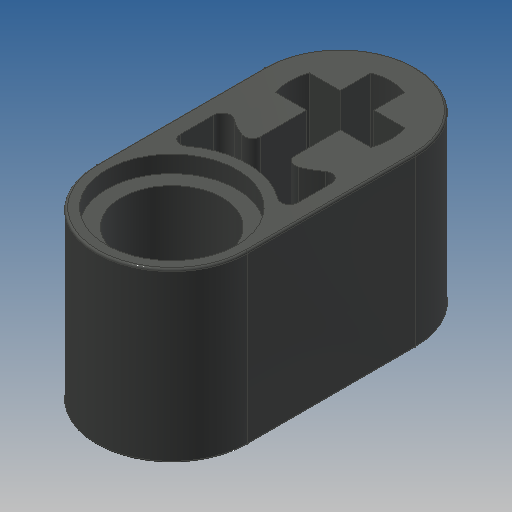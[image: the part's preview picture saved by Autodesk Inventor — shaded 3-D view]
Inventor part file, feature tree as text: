
AUTODESK INVENTOR PART (.ipt)
format: ipt  version: 2022.2 (Build 262287000, 287)  size: 195,072 bytes
history: native  units: mm
features: extrude x2, sketch x2, mirror x1, fillet x1
ambient origin geometry x8: Origin, YZ Plane, XZ Plane, XY Plane, X Axis, Y Axis, Z Axis, Center Point
bodies: Solid1 (feature_tree)
feature tree (6):
  extrude  "Extrusion1"  Depth=6.4mm
  extrude  "Extrusion7"  Depth=7.2mm
  mirror  "Mirror1"
  fillet  "Fillet1"  Radius=8.0mm
  sketch  "Sketch1"  dims[d8=4.8mm d9=6.4mm]
  sketch  "Sketch6"  dims[d14=8.0mm d15=0.0mm d32=7.2mm d34=8.0mm d36=0.8mm d41=0.8mm d42=0.0mm d45=0.1mm d46=0.4mm d52=1.6mm d53=6.2mm]
